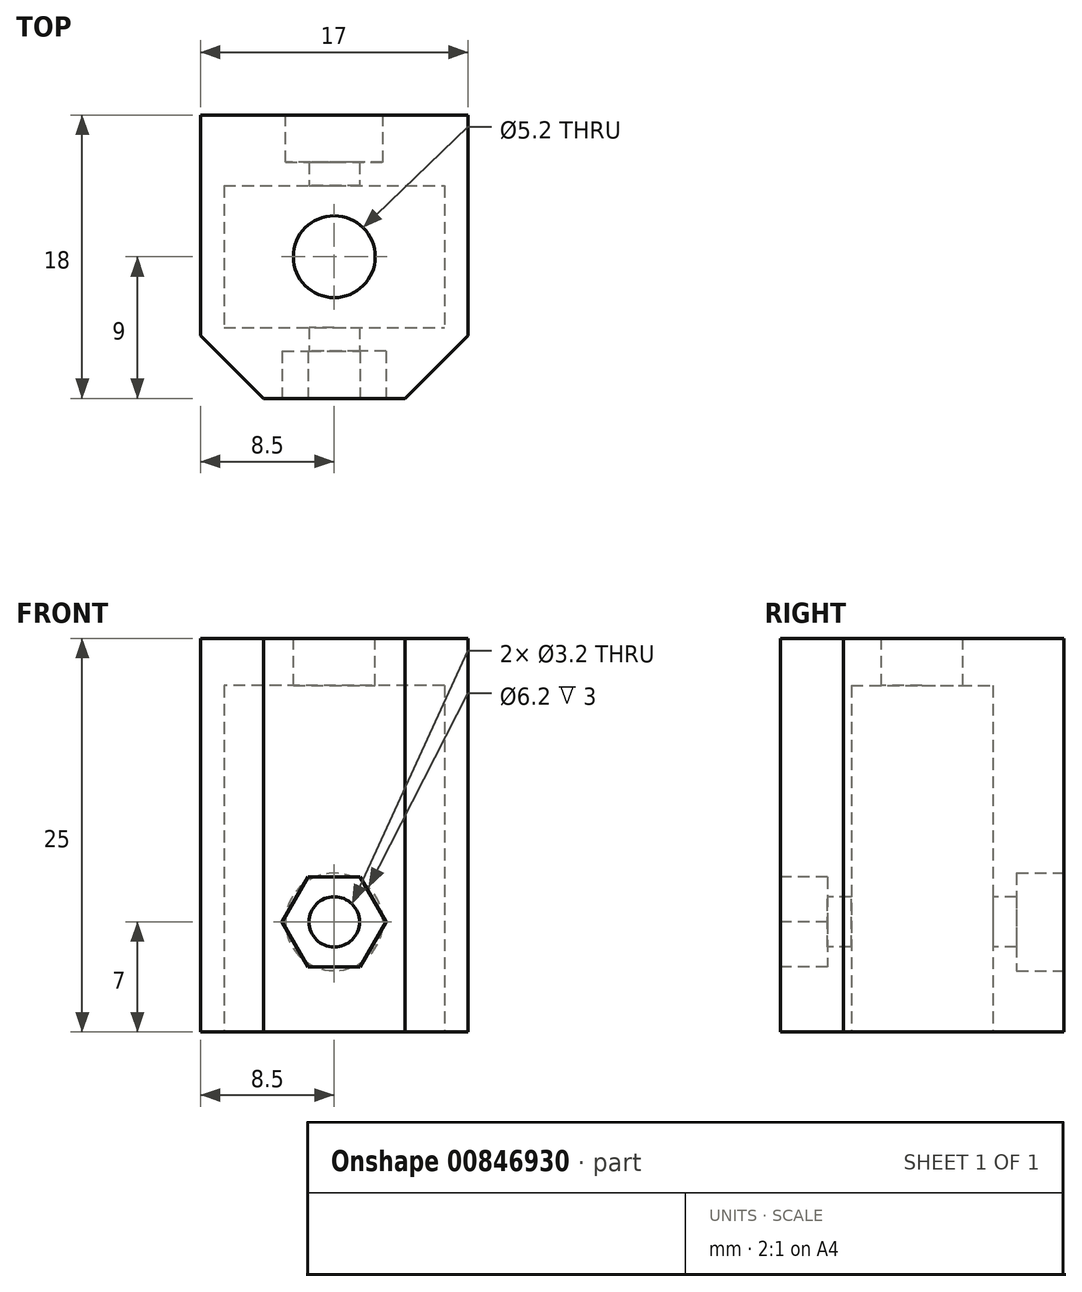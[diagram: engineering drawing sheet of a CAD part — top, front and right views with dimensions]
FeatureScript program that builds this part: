
annotation { "Feature Type Name" : "Feature", "Feature Type Description" : "" }
export const myFeature = defineFeature(function(context is Context, id is Id, definition is map)
    precondition{}
    {
        {
            var Q0;
            Q0=qCreatedBy(makeId("Front.planeOp"),FACE);
            var sketch = newSketch(context, id + "F0", { "sketchPlane" : qUnion([Q0])});
            skLineSegment(sketch, "E0.bottom", {"start": v(8.5, -12.5) * mm, "end": v(-8.5, -12.5) * mm});
            skLineSegment(sketch, "E0.top", {"start": v(8.5, 12.5) * mm, "end": v(-8.5, 12.5) * mm});
            skLineSegment(sketch, "E0.left", {"start": v(8.5, -12.5) * mm, "end": v(8.5, 12.5) * mm});
            skLineSegment(sketch, "E0.right", {"start": v(-8.5, -12.5) * mm, "end": v(-8.5, 12.5) * mm});
            skPoint(sketch, "E0.middle", {"position": v(0, 0) * mm});
            skSolve(sketch);
        }
        {
            var Q0;
            Q0 = qSketchRegion(id + "F0", true);
            extrude(context, id + "F1", {"entities" : qUnion([Q0]), "depth" : 18 * mm, "offsetDistance" : 25 * mm});
        }
        {
            var Q0;
            Q0=makeQuery(id+"F1.opExtrude","SWEPT_FACE",FACE,{"disambiguationData":[OSD([sQuery(id+"F0.wireOp",EDGE,"E0.bottom")])]});
            var sketch = newSketch(context, id + "F2", { "sketchPlane" : qUnion([Q0])});
            skLineSegment(sketch, "E1", {"start": v(-8.5, 0) * mm, "end": v(8.5, 18) * mm, "construction": true});
            skPoint(sketch, "E2", {"position": v(0, 9) * mm});
            skLineSegment(sketch, "E3.bottom", {"start": v(-7, 4.5) * mm, "end": v(7, 4.5) * mm});
            skLineSegment(sketch, "E3.top", {"start": v(-7, 13.5) * mm, "end": v(7, 13.5) * mm});
            skLineSegment(sketch, "E3.left", {"start": v(-7, 4.5) * mm, "end": v(-7, 13.5) * mm});
            skLineSegment(sketch, "E3.right", {"start": v(7, 4.5) * mm, "end": v(7, 13.5) * mm});
            skSolve(sketch);
        }
        {
            var Q0;
            Q0 = qSketchRegion(id + "F2", true);
            var Q1;
            Q1=makeQuery(id+"F1.opExtrude","SWEPT_FACE",FACE,{"disambiguationData":[OSD([sQuery(id+"F0.wireOp",EDGE,"E0.top")])]});
            extrude(context, id + "F3", {"entities" : qUnion([Q0]), "operationType" : NewBodyOperationType.REMOVE, "endBound" : BoundingType.UP_TO_SURFACE, "oppositeDirection" : true, "depth" : 25 * mm, "endBoundEntityFace" : qUnion([Q1]), "hasOffset" : true, "offsetDistance" : 3 * mm});
        }
        {
            var Q0;
            Q0=makeQuery(id+"F1.opExtrude","CAP_FACE",FACE,{"disambiguationData":[OSD([sQuery(id+"F0.wireOp",EDGE,"E0.bottom"),sQuery(id+"F0.wireOp",EDGE,"E0.top"),sQuery(id+"F0.wireOp",EDGE,"E0.left"),sQuery(id+"F0.wireOp",EDGE,"E0.right")])],"isStart":false});
            var sketch = newSketch(context, id + "F4", { "sketchPlane" : qUnion([Q0])});
            skPoint(sketch, "E4", {"position": v(0, -5.5) * mm});
            skPoint(sketch, "E4.positionSnap0", {"position": v(0, -12.5) * mm});
            skCircle(sketch, "E5", {"center": v(0, -5.5) * mm, "radius": 1.6 * mm});
            skSolve(sketch);
        }
        {
            var Q0;
            Q0 = qSketchRegion(id + "F4", true);
            extrude(context, id + "F5", {"entities" : qUnion([Q0]), "operationType" : NewBodyOperationType.REMOVE, "oppositeDirection" : true, "depth" : 25 * mm, "offsetDistance" : 25 * mm});
        }
        {
            var Q0;
            Q0=makeQuery(id+"F1.opExtrude","SWEPT_FACE",FACE,{"disambiguationData":[OSD([sQuery(id+"F0.wireOp",EDGE,"E0.top")])]});
            var sketch = newSketch(context, id + "F6", { "sketchPlane" : qUnion([Q0])});
            skLineSegment(sketch, "E6", {"start": v(-8.5, 0) * mm, "end": v(8.5, -18) * mm, "construction": true});
            skCircle(sketch, "E7", {"center": v(0, -9) * mm, "radius": 2.6 * mm});
            skSolve(sketch);
        }
        {
            var Q0;
            Q0 = qSketchRegion(id + "F6", true);
            extrude(context, id + "F7", {"entities" : qUnion([Q0]), "operationType" : NewBodyOperationType.REMOVE, "oppositeDirection" : true, "depth" : 25 * mm, "offsetDistance" : 25 * mm});
        }
        {
            var Q0;
            Q0=makeQuery(id+"F1.opExtrude","CAP_FACE",FACE,{"disambiguationData":[OSD([sQuery(id+"F0.wireOp",EDGE,"E0.bottom"),sQuery(id+"F0.wireOp",EDGE,"E0.top"),sQuery(id+"F0.wireOp",EDGE,"E0.left"),sQuery(id+"F0.wireOp",EDGE,"E0.right")])],"isStart":true});
            var sketch = newSketch(context, id + "F8", { "sketchPlane" : qUnion([Q0])});
            skCircle(sketch, "E8.0", {"center": v(0, -5.5) * mm, "radius": 1.6 * mm, "construction": true});
            skCircle(sketch, "E9", {"center": v(0, -5.5) * mm, "radius": 3.1 * mm});
            skSolve(sketch);
        }
        {
            var Q0;
            Q0 = qSketchRegion(id + "F8", true);
            extrude(context, id + "F9", {"entities" : qUnion([Q0]), "operationType" : NewBodyOperationType.REMOVE, "oppositeDirection" : true, "depth" : 3 * mm, "offsetDistance" : 25 * mm});
        }
        {
            var Q0;
            Q0=makeQuery(id+"F1.opExtrude","CAP_FACE",FACE,{"disambiguationData":[OSD([sQuery(id+"F0.wireOp",EDGE,"E0.bottom"),sQuery(id+"F0.wireOp",EDGE,"E0.top"),sQuery(id+"F0.wireOp",EDGE,"E0.left"),sQuery(id+"F0.wireOp",EDGE,"E0.right")])],"isStart":false});
            var sketch = newSketch(context, id + "F10", { "sketchPlane" : qUnion([Q0])});
            skCircle(sketch, "E10.0", {"center": v(0, -5.5) * mm, "radius": 1.6 * mm, "construction": true});
            skCircle(sketch, "E11.cCircle", {"center": v(0, -5.5) * mm, "radius": 2.86 * mm, "construction": true});
            skLineSegment(sketch, "E11.0", {"start": v(1.65, -8.36) * mm, "end": v(-1.65, -8.36) * mm});
            skLineSegment(sketch, "E11.1", {"start": v(-1.65, -8.36) * mm, "end": v(-3.3, -5.5) * mm});
            skLineSegment(sketch, "E11.2", {"start": v(-3.3, -5.5) * mm, "end": v(-1.65, -2.64) * mm});
            skLineSegment(sketch, "E11.3", {"start": v(-1.65, -2.64) * mm, "end": v(1.65, -2.64) * mm});
            skLineSegment(sketch, "E11.4", {"start": v(1.65, -2.64) * mm, "end": v(3.3, -5.5) * mm});
            skLineSegment(sketch, "E11.5", {"start": v(3.3, -5.5) * mm, "end": v(1.65, -8.36) * mm});
            skPoint(sketch, "E11.0.midPoint", {"position": v(0, -8.36) * mm});
            skSolve(sketch);
        }
        {
            var Q0;
            Q0 = qSketchRegion(id + "F10", true);
            extrude(context, id + "F11", {"entities" : qUnion([Q0]), "operationType" : NewBodyOperationType.REMOVE, "oppositeDirection" : true, "depth" : 3 * mm, "offsetDistance" : 25 * mm});
        }
        {
            var Q0;
            Q0=makeQuery(id+"F1.opExtrude","CAP_EDGE",EDGE,{"disambiguationData":[OSD([sQuery(id+"F0.wireOp",EDGE,"E0.left")])],"isStart":false});
            var Q1;
            Q1=makeQuery(id+"F1.opExtrude","CAP_EDGE",EDGE,{"disambiguationData":[OSD([sQuery(id+"F0.wireOp",EDGE,"E0.right")])],"isStart":false});
            chamfer(context, id + "F12", {"entities" : qUnion([Q0, Q1]), "width" : 4 * mm, "tangentPropagation" : true});
        }
    });
